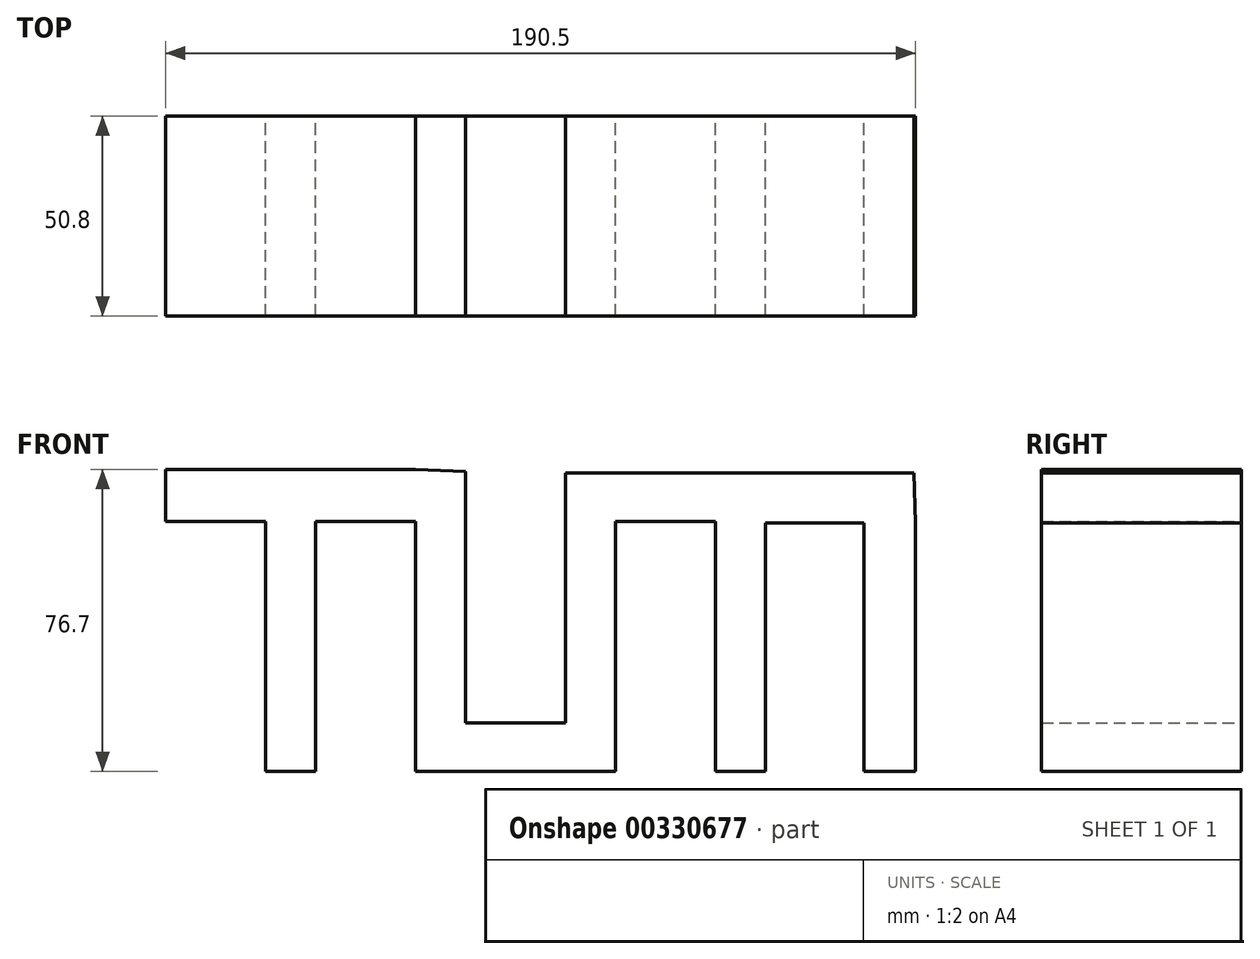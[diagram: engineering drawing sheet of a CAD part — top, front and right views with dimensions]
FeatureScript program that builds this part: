
annotation { "Feature Type Name" : "Feature", "Feature Type Description" : "" }
export const myFeature = defineFeature(function(context is Context, id is Id, definition is map)
    precondition{}
    {
        {
            var Q0;
            Q0=qCreatedBy(makeId("Front.planeOp"),FACE);
            var sketch = newSketch(context, id + "F0", { "sketchPlane" : qUnion([Q0])});
            skLineSegment(sketch, "E0.top", {"start": v(-111.16, 25.4) * mm, "end": v(-98.46, 25.4) * mm});
            skLineSegment(sketch, "E0.left", {"start": v(-111.16, 88.9) * mm, "end": v(-111.16, 25.4) * mm});
            skLineSegment(sketch, "E0.right", {"start": v(-98.46, 88.9) * mm, "end": v(-98.46, 25.4) * mm});
            skLineSegment(sketch, "E1.bottom", {"start": v(-136.56, 102.1) * mm, "end": v(-73.06, 102.1) * mm});
            skLineSegment(sketch, "E1.top", {"start": v(-136.56, 88.9) * mm, "end": v(-111.16, 88.9) * mm});
            skLineSegment(sketch, "E1.left", {"start": v(-136.56, 102.1) * mm, "end": v(-136.56, 88.9) * mm});
            skLineSegment(sketch, "E2.left", {"start": v(-73.06, 88.9) * mm, "end": v(-73.06, 25.4) * mm});
            skLineSegment(sketch, "E3.bottom", {"start": v(-60.37, 37.68) * mm, "end": v(-34.97, 37.68) * mm});
            skLineSegment(sketch, "E3.top", {"start": v(-60.37, 25.4) * mm, "end": v(-22.26, 25.4) * mm});
            skLineSegment(sketch, "E4.left", {"start": v(-22.26, 25.4) * mm, "end": v(-22.26, 88.9) * mm});
            skLineSegment(sketch, "E4.right", {"start": v(-34.97, 37.68) * mm, "end": v(-34.97, 101.18) * mm});
            skLineSegment(sketch, "E5.bottom", {"start": v(-22.26, 101.18) * mm, "end": v(3.14, 101.18) * mm});
            skLineSegment(sketch, "E5.top", {"start": v(-22.26, 88.9) * mm, "end": v(3.14, 88.9) * mm});
            skLineSegment(sketch, "E6.bottom", {"start": v(3.14, 101.18) * mm, "end": v(15.84, 101.18) * mm});
            skLineSegment(sketch, "E6.top", {"start": v(3.14, 25.4) * mm, "end": v(15.84, 25.4) * mm});
            skLineSegment(sketch, "E6.left", {"start": v(3.14, 88.9) * mm, "end": v(3.14, 25.4) * mm});
            skLineSegment(sketch, "E6.right", {"start": v(15.84, 88.48) * mm, "end": v(15.84, 25.4) * mm});
            skLineSegment(sketch, "E7.bottom", {"start": v(15.84, 101.18) * mm, "end": v(40.85, 101.18) * mm});
            skLineSegment(sketch, "E7.top", {"start": v(15.84, 88.48) * mm, "end": v(40.85, 88.48) * mm});
            skLineSegment(sketch, "E8.top", {"start": v(53.94, 25.4) * mm, "end": v(40.85, 25.4) * mm});
            skLineSegment(sketch, "E8.left", {"start": v(53.94, 88.48) * mm, "end": v(53.94, 25.4) * mm});
            skLineSegment(sketch, "E8.right", {"start": v(40.85, 88.48) * mm, "end": v(40.85, 25.4) * mm});
            skLineSegment(sketch, "E9.trimOffspring", {"start": v(-98.46, 88.9) * mm, "end": v(-73.06, 88.9) * mm});
            skLineSegment(sketch, "E10", {"start": v(40.85, 101.18) * mm, "end": v(53.55, 101.18) * mm});
            skPoint(sketch, "E1.right.end.orphan", {"position": v(-60.37, 88.9) * mm});
            skLineSegment(sketch, "E11", {"start": v(-60.37, 101.6) * mm, "end": v(-73.06, 102.1) * mm});
            skLineSegment(sketch, "E12", {"start": v(-60.37, 101.6) * mm, "end": v(-60.37, 37.68) * mm});
            skLineSegment(sketch, "E13", {"start": v(-73.06, 25.4) * mm, "end": v(-60.37, 25.4) * mm});
            skLineSegment(sketch, "E14", {"start": v(-34.97, 101.18) * mm, "end": v(-22.26, 101.18) * mm});
            skLineSegment(sketch, "E15", {"start": v(53.55, 101.18) * mm, "end": v(53.94, 88.48) * mm});
            skSolve(sketch);
        }
        {
            var Q0;
            Q0 = qSketchRegion(id + "F0", true);
            extrude(context, id + "F1", {"entities" : qUnion([Q0]), "depth" : 25.4 * mm});
        }
        {
            var Q0;
            Q0 = qSketchRegion(id + "F0", true);
            extrude(context, id + "F2", {"entities" : qUnion([Q0]), "operationType" : NewBodyOperationType.ADD, "depth" : 50.8 * mm});
        }
    });
